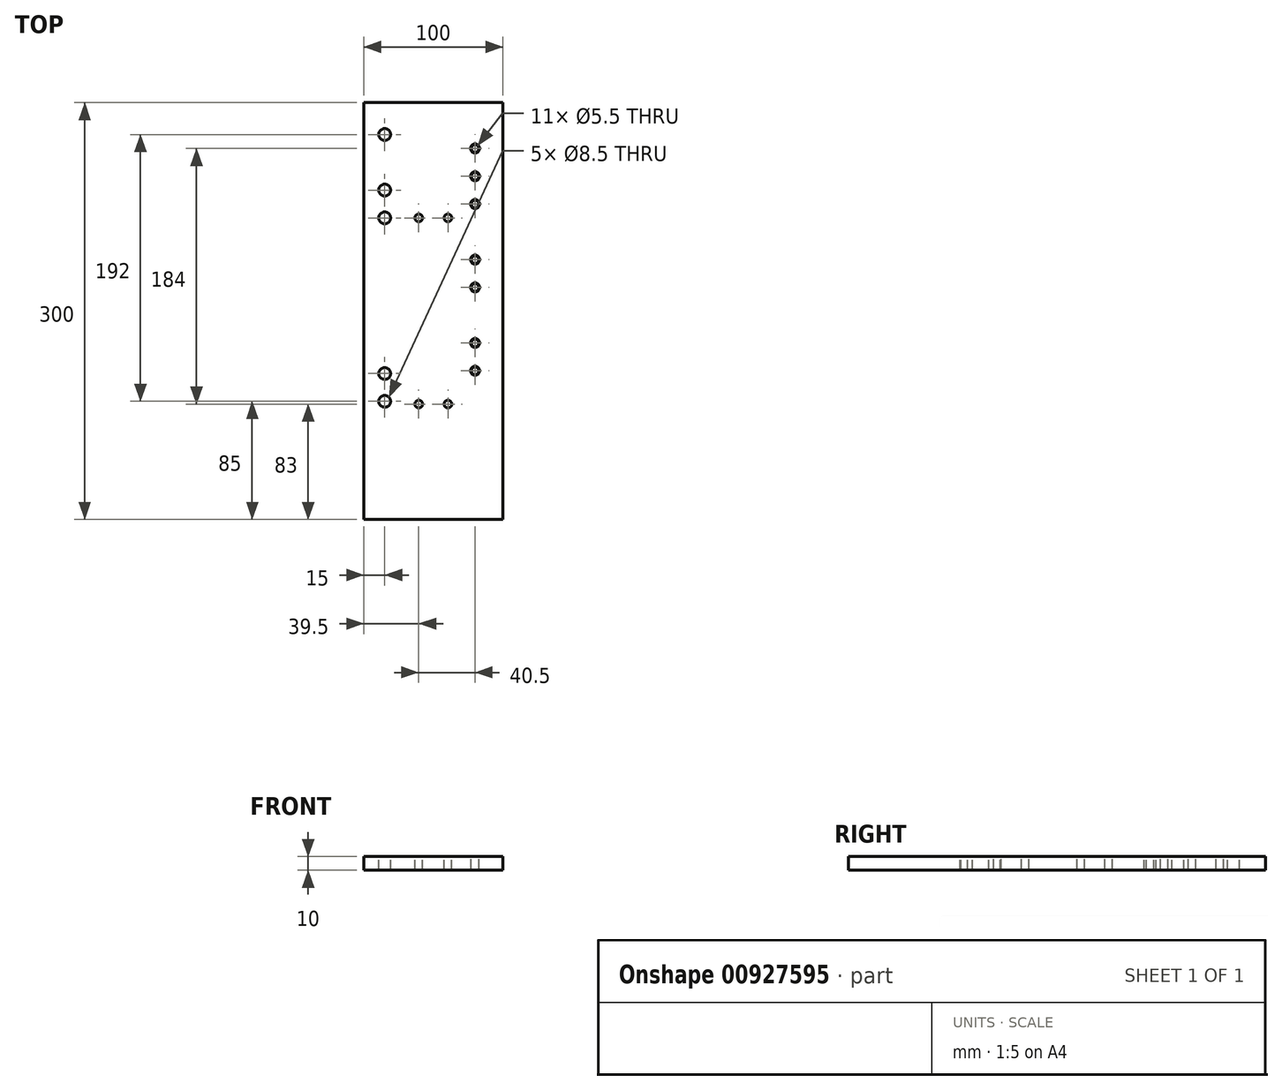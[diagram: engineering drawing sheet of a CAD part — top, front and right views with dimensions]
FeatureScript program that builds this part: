
annotation { "Feature Type Name" : "Feature", "Feature Type Description" : "" }
export const myFeature = defineFeature(function(context is Context, id is Id, definition is map)
    precondition{}
    {
        {
            var Q0;
            Q0=qCreatedBy(makeId("Right.planeOp"),FACE);
            var sketch = newSketch(context, id + "F0", { "sketchPlane" : qUnion([Q0])});
            skLineSegment(sketch, "E0.bottom", {"start": v(-300, 10) * mm, "end": v(0, 10) * mm});
            skLineSegment(sketch, "E0.top", {"start": v(-300, 0) * mm, "end": v(0, 0) * mm});
            skLineSegment(sketch, "E0.left", {"start": v(-300, 10) * mm, "end": v(-300, 0) * mm});
            skLineSegment(sketch, "E0.right", {"start": v(0, 10) * mm, "end": v(0, 0) * mm});
            skSolve(sketch);
        }
        {
            var Q0;
            Q0=makeQuery(id+"F0.imprint","IMPRINT",FACE,{"disambiguationData":[TD([[makeQuery(id+"F0.imprint","IMPRINT",EDGE,{"derivedFrom":sQuery(id+"F0.wireOp",EDGE,"E0.bottom")}),-1.0]])]});
            extrude(context, id + "F1", {"entities" : qUnion([Q0]), "depth" : 100 * mm, "offsetDistance" : 25 * mm});
        }
        {
            var Q0;
            Q0=makeQuery(id+"F1.opExtrude","SWEPT_FACE",FACE,{"disambiguationData":[OSD([sQuery(id+"F0.wireOp",EDGE,"E0.bottom")])]});
            var sketch = newSketch(context, id + "F2", { "sketchPlane" : qUnion([Q0])});
            skLineSegment(sketch, "E1", {"start": v(-81.81, -150) * mm, "end": v(149.72, -150) * mm, "construction": true});
            skPoint(sketch, "E1.startSnap0", {"position": v(0, -150) * mm});
            skLineSegment(sketch, "E2", {"start": v(-90.3, -83) * mm, "end": v(189.33, -83) * mm, "construction": true});
            skLineSegment(sketch, "E3.MirrorCS", {"start": v(-90.3, -217) * mm, "end": v(189.33, -217) * mm, "construction": true});
            skCircle(sketch, "E4", {"center": v(60.5, -83) * mm, "radius": 2.75 * mm});
            skLineSegment(sketch, "E5", {"start": v(50, 23.78) * mm, "end": v(50, -331.3) * mm, "construction": true});
            skPoint(sketch, "E5.startSnap0", {"position": v(50, 0) * mm});
            skPoint(sketch, "E5.endSnap0", {"position": v(50, -300) * mm});
            skCircle(sketch, "E6.MirrorC", {"center": v(39.5, -83) * mm, "radius": 2.75 * mm});
            skCircle(sketch, "E7.MirrorC", {"center": v(39.5, -217) * mm, "radius": 2.75 * mm});
            skCircle(sketch, "E8.MirrorC", {"center": v(60.5, -217) * mm, "radius": 2.75 * mm});
            skLineSegment(sketch, "E9", {"start": v(15, -16.67) * mm, "end": v(15, -268.55) * mm, "construction": true});
            skCircle(sketch, "E10", {"center": v(15, -215) * mm, "radius": 4.25 * mm});
            skCircle(sketch, "E11", {"center": v(15, -195) * mm, "radius": 4.25 * mm});
            skCircle(sketch, "E12", {"center": v(15, -83) * mm, "radius": 4.25 * mm});
            skCircle(sketch, "E13", {"center": v(15, -63) * mm, "radius": 4.25 * mm});
            skCircle(sketch, "E14", {"center": v(15, -23) * mm, "radius": 4.25 * mm});
            skSolve(sketch);
        }
        {
            var Q0;
            Q0 = qSketchRegion(id + "F2", true);
            extrude(context, id + "F3", {"entities" : qUnion([Q0]), "operationType" : NewBodyOperationType.REMOVE, "endBound" : BoundingType.THROUGH_ALL, "oppositeDirection" : true, "depth" : 25 * mm, "offsetDistance" : 25 * mm});
        }
        {
            var Q0;
            Q0=makeQuery(id+"F1.opExtrude","SWEPT_FACE",FACE,{"disambiguationData":[OSD([sQuery(id+"F0.wireOp",EDGE,"E0.bottom")])]});
            var sketch = newSketch(context, id + "F4", { "sketchPlane" : qUnion([Q0])});
            skLineSegment(sketch, "E15", {"start": v(80, 12.93) * mm, "end": v(80, -320.46) * mm, "construction": true});
            skLineSegment(sketch, "E16", {"start": v(-50.69, -193) * mm, "end": v(209.14, -193) * mm, "construction": true});
            skCircle(sketch, "E17", {"center": v(80, -193) * mm, "radius": 2.75 * mm});
            skLineSegment(sketch, "E18", {"start": v(13.97, -173) * mm, "end": v(196.11, -173) * mm, "construction": true});
            skLineSegment(sketch, "E19", {"start": v(42.96, -133) * mm, "end": v(144.6, -133) * mm, "construction": true});
            skLineSegment(sketch, "E20", {"start": v(45.18, -113) * mm, "end": v(144.55, -113) * mm, "construction": true});
            skLineSegment(sketch, "E21", {"start": v(48.92, -73) * mm, "end": v(140.75, -73) * mm, "construction": true});
            skLineSegment(sketch, "E22", {"start": v(52.53, -53) * mm, "end": v(141.39, -53) * mm, "construction": true});
            skCircle(sketch, "E23", {"center": v(80, -173) * mm, "radius": 2.75 * mm});
            skCircle(sketch, "E24", {"center": v(80, -133) * mm, "radius": 2.75 * mm});
            skCircle(sketch, "E25", {"center": v(80, -113) * mm, "radius": 2.75 * mm});
            skCircle(sketch, "E26", {"center": v(80, -73) * mm, "radius": 2.75 * mm});
            skCircle(sketch, "E27", {"center": v(80, -53) * mm, "radius": 2.75 * mm});
            skLineSegment(sketch, "E28", {"start": v(60.43, -33) * mm, "end": v(111.66, -33) * mm, "construction": true});
            skCircle(sketch, "E29", {"center": v(80, -33) * mm, "radius": 2.75 * mm});
            skSolve(sketch);
        }
        {
            var Q0;
            Q0 = qSketchRegion(id + "F4", true);
            extrude(context, id + "F5", {"entities" : qUnion([Q0]), "operationType" : NewBodyOperationType.REMOVE, "endBound" : BoundingType.THROUGH_ALL, "oppositeDirection" : true, "depth" : 25 * mm, "offsetDistance" : 25 * mm});
        }
        {
            var Q0;
            Q0=makeQuery(id+"F5.boolean.opBoolean","COPY",FACE,{"derivedFrom":makeQuery(id+"F5.opExtrude","SWEPT_FACE",FACE,{"disambiguationData":[OSD([sQuery(id+"F4.wireOp",EDGE,"E27")])]})});
            var Q1;
            Q1=makeQuery(id+"F5.boolean.opBoolean","COPY",FACE,{"derivedFrom":makeQuery(id+"F5.opExtrude","SWEPT_FACE",FACE,{"disambiguationData":[OSD([sQuery(id+"F4.wireOp",EDGE,"E26")])]})});
            var Q2;
            Q2=makeQuery(id+"F5.boolean.opBoolean","COPY",FACE,{"derivedFrom":makeQuery(id+"F5.opExtrude","SWEPT_FACE",FACE,{"disambiguationData":[OSD([sQuery(id+"F4.wireOp",EDGE,"E25")])]})});
            var Q3;
            Q3=makeQuery(id+"F5.boolean.opBoolean","COPY",FACE,{"derivedFrom":makeQuery(id+"F5.opExtrude","SWEPT_FACE",FACE,{"disambiguationData":[OSD([sQuery(id+"F4.wireOp",EDGE,"E24")])]})});
            var Q4;
            Q4=makeQuery(id+"F5.boolean.opBoolean","COPY",FACE,{"derivedFrom":makeQuery(id+"F5.opExtrude","SWEPT_FACE",FACE,{"disambiguationData":[OSD([sQuery(id+"F4.wireOp",EDGE,"E23")])]})});
            var Q5;
            Q5=makeQuery(id+"F5.boolean.opBoolean","COPY",FACE,{"derivedFrom":makeQuery(id+"F5.opExtrude","SWEPT_FACE",FACE,{"disambiguationData":[OSD([sQuery(id+"F4.wireOp",EDGE,"E17")])]})});
            var Q6;
            Q6=makeQuery(id+"F5.boolean.opBoolean","COPY",FACE,{"derivedFrom":makeQuery(id+"F5.opExtrude","SWEPT_FACE",FACE,{"disambiguationData":[OSD([sQuery(id+"F4.wireOp",EDGE,"E29")])]})});
            chamfer(context, id + "F6", {"entities" : qUnion([Q0, Q1, Q2, Q3, Q4, Q5, Q6]), "width" : 0.5 * mm, "tangentPropagation" : true});
        }
    });
